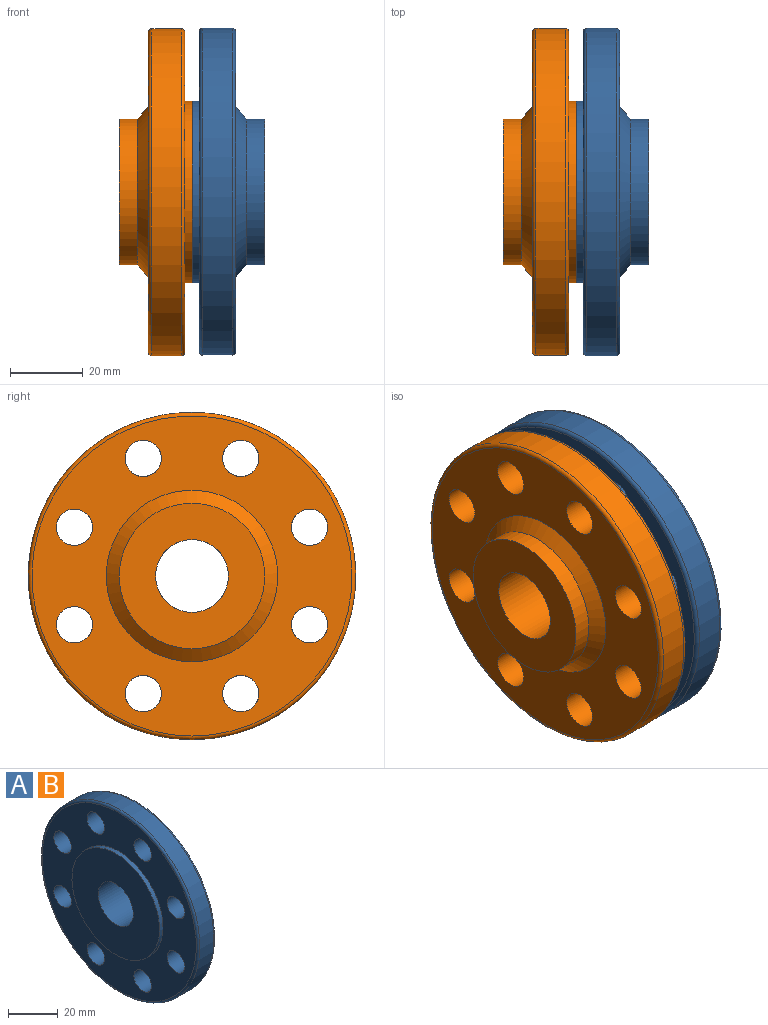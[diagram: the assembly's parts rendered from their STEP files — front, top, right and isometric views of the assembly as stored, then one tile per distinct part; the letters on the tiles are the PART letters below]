
ASSEMBLY  parts=2 mates=1
PART A: 19 faces, bbox 20x97.4x97.4 mm
  f0: cylinder r=20mm len=40mm, axis (-1,0,0), area 628.3mm2, adj f1,f10
  f1: cone r=23.58mm half-angle=50deg, axis (-1,0,0), area 638.9mm2, adj f0,f2
  f2: plane 88x88mm, normal (1,0,0), area 3707.7mm2, adj f1,f3,f11,f12,f13,f14,f15,f16
  f3: torus R=44mm, axis (-1,0,0), area 440.5mm2, adj f2,f4
  f4: cylinder r=45mm len=90mm, axis (-1,0,0), area 2261.9mm2, adj f3,f5
  f5: torus R=44mm, axis (-1,0,0), area 440.5mm2, adj f4,f6
  f6: plane 88x88mm, normal (-1,0,0), area 3490.3mm2, adj f5,f7,f11,f12,f13,f14,f15,f16
  f7: cylinder r=25mm len=50mm, axis (-1,0,0), area 314.2mm2, adj f6,f8
  f8: plane 50x50mm, normal (-1,0,0), area 1649.3mm2, adj f7,f9
  f9: cylinder r=10mm len=20mm, axis (-1,0,0), area 1256.6mm2, adj f8,f10
  f10: plane 40x40mm, normal (1,0,0), area 942.5mm2, adj f0,f9
  f11: cylinder r=5mm len=10mm, axis (-1,0,0), area 314.2mm2, adj f2,f6
  f12: cylinder r=5mm len=10mm, axis (-1,0,0), area 314.2mm2, adj f2,f6
  f13: cylinder r=5mm len=10mm, axis (-1,0,0), area 314.2mm2, adj f2,f6
  f14: cylinder r=5mm len=10mm, axis (-1,0,0), area 314.2mm2, adj f2,f6
  f15: cylinder r=5mm len=10mm, axis (-1,0,0), area 314.2mm2, adj f2,f6
  f16: cylinder r=5mm len=10mm, axis (-1,0,0), area 314.2mm2, adj f2,f6
  f17: cylinder r=5mm len=10mm, axis (-1,0,0), area 314.2mm2, adj f2,f6
  f18: cylinder r=5mm len=10mm, axis (-1,0,0), area 314.2mm2, adj f2,f6
PART B: same geometry as A
PLACE A t=(19.79,-8.83,-49.41)mm
PLACE B rot(axis=(0,1,0),180deg) t=(19.79,-8.83,-49.41)mm
MATE fastened B.f1 <-> A.f1  axis (1,0,0) through (19.79,-8.83,-49.41)mm
